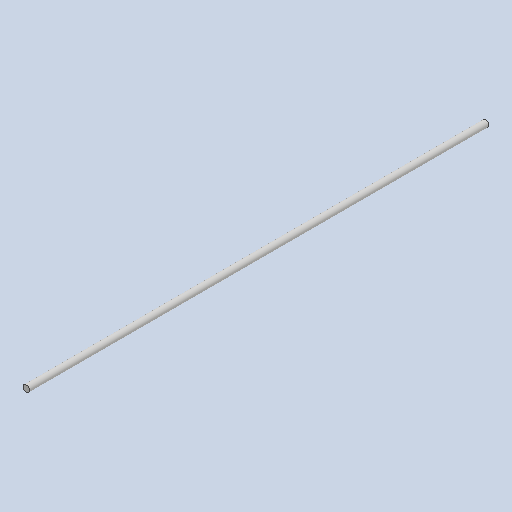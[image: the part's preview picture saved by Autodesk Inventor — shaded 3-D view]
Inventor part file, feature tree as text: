
AUTODESK INVENTOR PART (.ipt)
format: ipt  version: 2023 (Build 270158000, 158)  size: 80,896 bytes
history: native  units: mm
features: extrude x1, sketch x1
ambient origin geometry x8: Origin, YZ Plane, XZ Plane, XY Plane, X Axis, Y Axis, Z Axis, Center Point
bodies: Solid1 (feature_tree)
feature tree (2):
  extrude  "Extrusion1"  Depth=560.0mm
  sketch  "Sketch1"  dims[d0=8.0mm d1=560.0mm d2=0.0mm]
